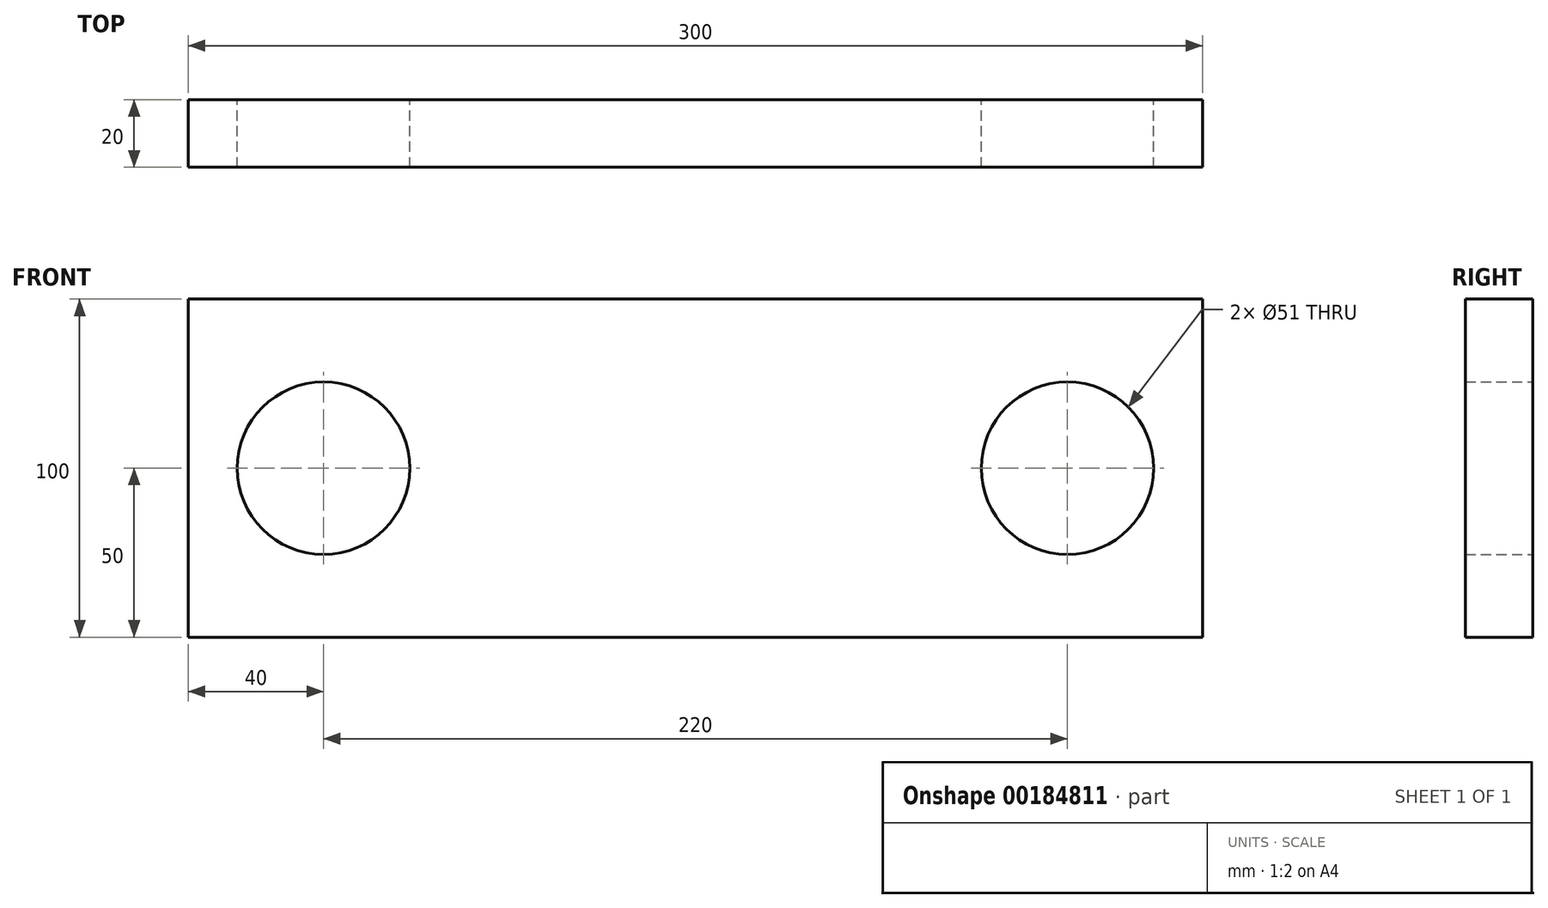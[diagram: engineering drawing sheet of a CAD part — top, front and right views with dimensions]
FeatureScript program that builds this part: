
annotation { "Feature Type Name" : "Feature", "Feature Type Description" : "" }
export const myFeature = defineFeature(function(context is Context, id is Id, definition is map)
    precondition{}
    {
        {
            var Q0;
            Q0=qCreatedBy(makeId("Front.planeOp"),FACE);
            var sketch = newSketch(context, id + "F0", { "sketchPlane" : qUnion([Q0])});
            skLineSegment(sketch, "E0.bottom", {"start": v(0, 0) * mm, "end": v(300, 0) * mm});
            skLineSegment(sketch, "E0.top", {"start": v(0, 100) * mm, "end": v(300, 100) * mm});
            skLineSegment(sketch, "E0.left", {"start": v(0, 0) * mm, "end": v(0, 100) * mm});
            skLineSegment(sketch, "E0.right", {"start": v(300, 0) * mm, "end": v(300, 100) * mm});
            skLineSegment(sketch, "E1", {"start": v(0, 50) * mm, "end": v(40, 50) * mm, "construction": true});
            skCircle(sketch, "E2", {"center": v(40, 50) * mm, "radius": 25.5 * mm});
            skLineSegment(sketch, "E3", {"start": v(300, 50) * mm, "end": v(260, 50) * mm, "construction": true});
            skPoint(sketch, "E3.endSnap0", {"position": v(300, 50) * mm});
            skCircle(sketch, "E4", {"center": v(260, 50) * mm, "radius": 25.5 * mm});
            skSolve(sketch);
        }
        {
            var Q0;
            Q0=makeQuery(id+"F0.imprint","IMPRINT",FACE,{"disambiguationData":[TD([[makeQuery(id+"F0.imprint","IMPRINT",EDGE,{"derivedFrom":sQuery(id+"F0.wireOp",EDGE,"E0.bottom")}),1.0]])]});
            extrude(context, id + "F1", {"entities" : qUnion([Q0]), "depth" : 20 * mm});
        }
    });
